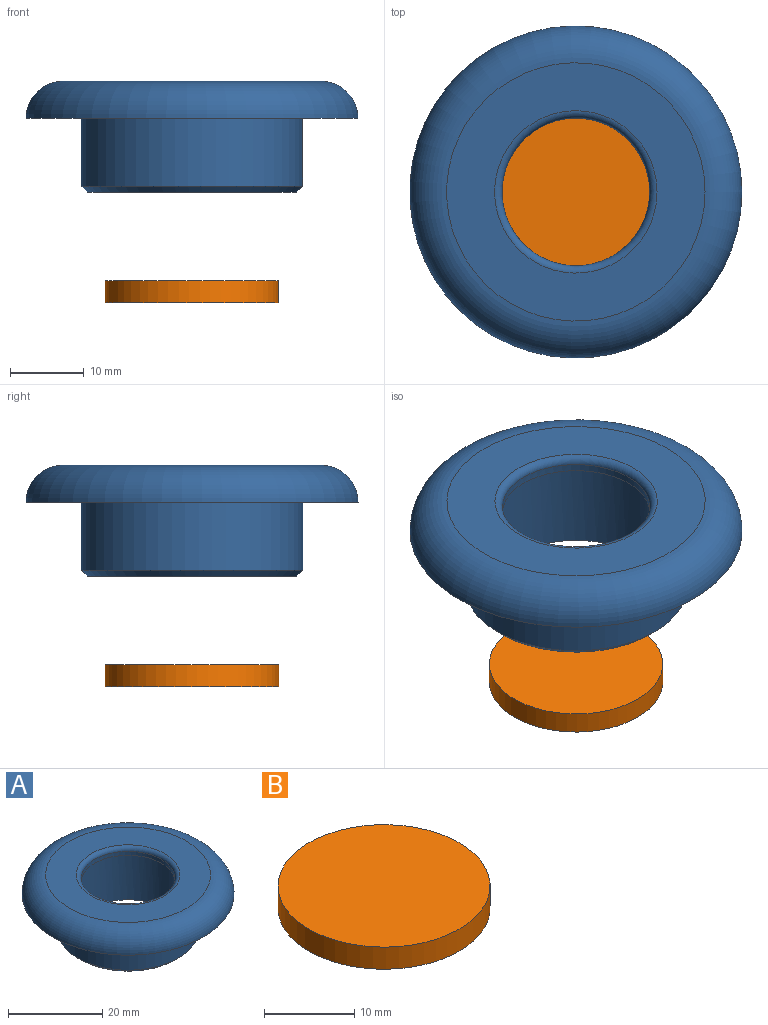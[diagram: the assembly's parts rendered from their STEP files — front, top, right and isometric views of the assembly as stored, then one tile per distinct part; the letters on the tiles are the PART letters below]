
ASSEMBLY  parts=2 mates=1
PART A: 10 faces, bbox 48.7x48.7x15 mm
  f0: cylinder r=10mm len=20mm, axis (0,0,1), area 62.8mm2, adj f7,f9
  f1: cylinder r=15mm len=30mm, axis (0,0,-1), area 867.1mm2, adj f3,f5
  f2: plane 28.4x28.4mm, normal (0,0,-1), area 181.1mm2, adj f3,f4
  f3: cone r=15mm half-angle=45deg, axis (0,0,1), area 103.8mm2, adj f1,f2
  f4: cylinder r=12mm len=24mm, axis (0,0,-1), area 980.2mm2, adj f2,f9
  f5: plane 45x45mm, normal (0,0,-1), area 883.6mm2, adj f1,f8
  f6: plane 35x35mm, normal (0,0,1), area 582mm2, adj f7,f8
  f7: torus R=11mm, axis (0,0,1), area 102.3mm2, adj f0,f6
  f8: torus R=17.5mm, axis (0,0,1), area 1020.7mm2, adj f5,f6
  f9: plane 24x24mm, normal (0,0,-1), area 138.2mm2, adj f0,f4
PART B: 3 faces, bbox 23.5x23.5x3 mm
  f0: cylinder r=11.75mm len=23.5mm, axis (0,0,-1), area 221.5mm2, adj f1,f2
  f1: plane 23.5x23.5mm, normal (0,0,1), area 433.7mm2, adj f0
  f2: plane 23.5x23.5mm, normal (0,0,-1), area 433.7mm2, adj f0
PLACE A t=(-8.44,-1.71,-2.75)mm
PLACE B t=(-8.44,-1.71,-17.75)mm
MATE cylindrical B.f0 <-> A.f4  axis (0,0,1) through (-8.44,-1.71,-14.75)mm
